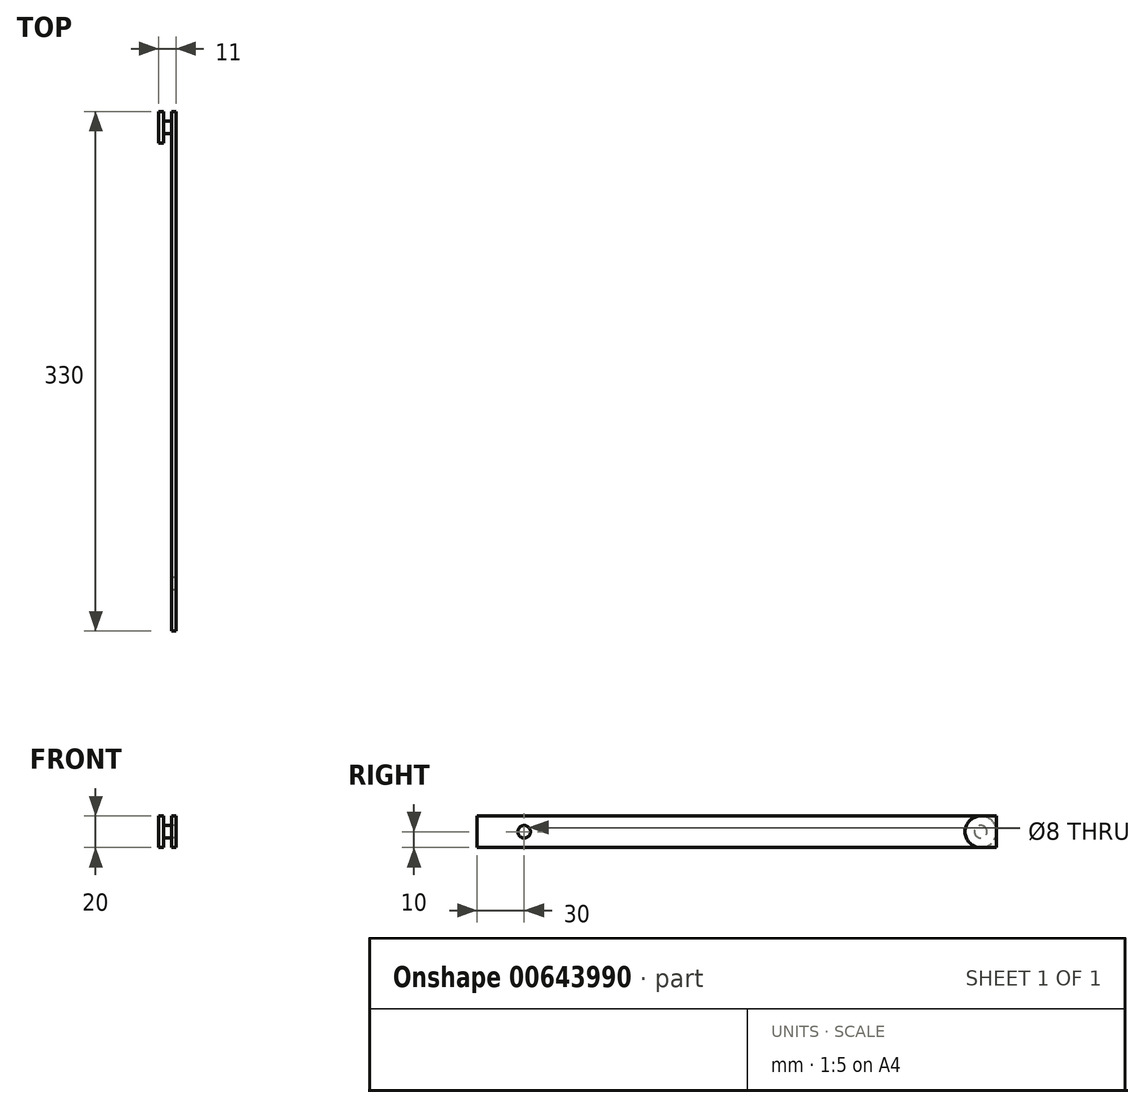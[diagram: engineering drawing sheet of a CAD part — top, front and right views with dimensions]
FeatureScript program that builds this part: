
annotation { "Feature Type Name" : "Feature", "Feature Type Description" : "" }
export const myFeature = defineFeature(function(context is Context, id is Id, definition is map)
    precondition{}
    {
        {
            var Q0;
            Q0=qCreatedBy(makeId("Right.planeOp"),FACE);
            var sketch = newSketch(context, id + "F0", { "sketchPlane" : qUnion([Q0])});
            skLineSegment(sketch, "E0", {"start": v(0, 0) * mm, "end": v(330, 0) * mm});
            skLineSegment(sketch, "E1", {"start": v(330, 0) * mm, "end": v(330, 20) * mm});
            skLineSegment(sketch, "E2", {"start": v(330, 20) * mm, "end": v(0, 20) * mm});
            skLineSegment(sketch, "E3", {"start": v(0, 20) * mm, "end": v(0, 0) * mm});
            skCircle(sketch, "E4", {"center": v(30, 10) * mm, "radius": 4 * mm});
            skCircle(sketch, "E5", {"center": v(320, 10) * mm, "radius": 4 * mm});
            skSolve(sketch);
        }
        {
            var Q0;
            Q0=makeQuery(id+"F0.imprint","IMPRINT",FACE,{"disambiguationData":[TD([[makeQuery(id+"F0.imprint","IMPRINT",EDGE,{"derivedFrom":sQuery(id+"F0.wireOp",EDGE,"E0")}),1.0]])]});
            var Q1;
            Q1=makeQuery(id+"F0.imprint","IMPRINT",FACE,{"disambiguationData":[TD([[makeQuery(id+"F0.imprint","IMPRINT",EDGE,{"derivedFrom":sQuery(id+"F0.wireOp",EDGE,"E5")}),1.0]])]});
            extrude(context, id + "F1", {"entities" : qUnion([Q0, Q1]), "depth" : 3 * mm, "offsetDistance" : 25 * mm});
        }
        {
            var Q0;
            Q0=makeQuery(id+"F0.imprint","IMPRINT",FACE,{"disambiguationData":[TD([[makeQuery(id+"F0.imprint","IMPRINT",EDGE,{"derivedFrom":sQuery(id+"F0.wireOp",EDGE,"E5")}),1.0]])]});
            extrude(context, id + "F2", {"entities" : qUnion([Q0]), "operationType" : NewBodyOperationType.ADD, "oppositeDirection" : true, "depth" : 5 * mm, "offsetDistance" : 25 * mm});
        }
        {
            var Q0;
            Q0=qCreatedBy(makeId("Right.planeOp"),FACE);
            cPlane(context, id + "F3", {"entities" : qUnion([Q0]), "cplaneType" : CPlaneType.OFFSET, "offset" : 5 * mm, "oppositeDirection" : true, "width" : 150 * mm, "height" : 150 * mm});
        }
        {
            var Q0;
            Q0=qCreatedBy(id+"F3.planeOp",FACE);
            var sketch = newSketch(context, id + "F4", { "sketchPlane" : qUnion([Q0])});
            skPoint(sketch, "E6", {"position": v(320, 10) * mm});
            skCircle(sketch, "E7", {"center": v(320, 10) * mm, "radius": 10 * mm});
            skSolve(sketch);
        }
        {
            var Q0;
            Q0 = qSketchRegion(id + "F4", true);
            extrude(context, id + "F5", {"entities" : qUnion([Q0]), "operationType" : NewBodyOperationType.ADD, "oppositeDirection" : true, "depth" : 3 * mm, "offsetDistance" : 25 * mm});
        }
    });
